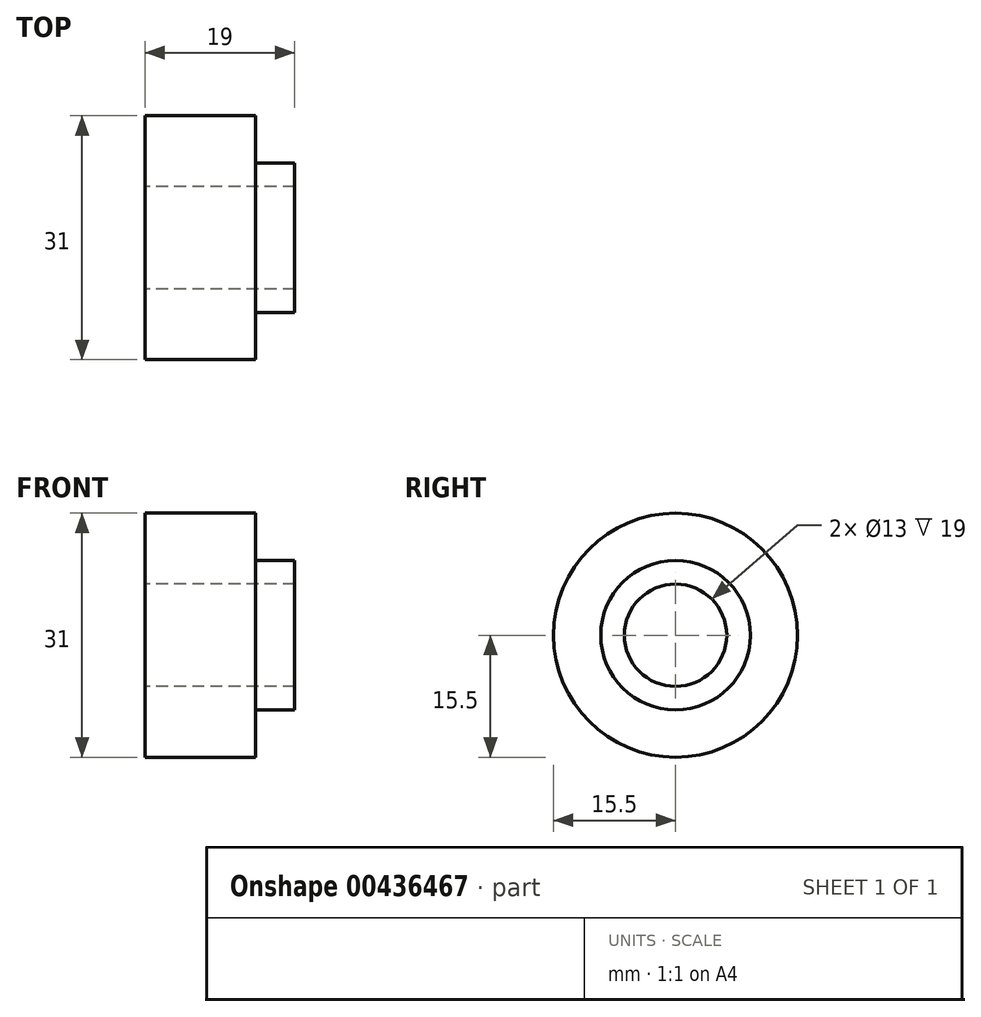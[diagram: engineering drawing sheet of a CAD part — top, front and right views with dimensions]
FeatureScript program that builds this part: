
annotation { "Feature Type Name" : "Feature", "Feature Type Description" : "" }
export const myFeature = defineFeature(function(context is Context, id is Id, definition is map)
    precondition{}
    {
        {
            var Q0;
            Q0=qCreatedBy(makeId("Front.planeOp"),FACE);
            var sketch = newSketch(context, id + "F0", { "sketchPlane" : qUnion([Q0])});
            skLineSegment(sketch, "E0", {"start": v(19, 6.5) * mm, "end": v(0, 6.5) * mm});
            skLineSegment(sketch, "E1", {"start": v(0, 6.5) * mm, "end": v(0, 15.5) * mm});
            skLineSegment(sketch, "E2", {"start": v(0, 15.5) * mm, "end": v(14, 15.5) * mm});
            skLineSegment(sketch, "E3", {"start": v(14, 15.5) * mm, "end": v(14, 9.5) * mm});
            skLineSegment(sketch, "E4", {"start": v(14, 9.5) * mm, "end": v(19, 9.5) * mm});
            skLineSegment(sketch, "E5", {"start": v(19, 9.5) * mm, "end": v(19, 6.5) * mm});
            skLineSegment(sketch, "E6", {"start": v(-70.83, 0) * mm, "end": v(70.83, 0) * mm});
            skSolve(sketch);
        }
        {
            var Q0;
            Q0 = qSketchRegion(id + "F0", true);
            var Q1;
            Q1=sQuery(id+"F0.wireOp",EDGE,"E6");
            revolve(context, id + "F1", {"entities" : qUnion([Q0]), "axis" : qUnion([Q1]), "revolveType" : RevolveType.FULL});
        }
    });
